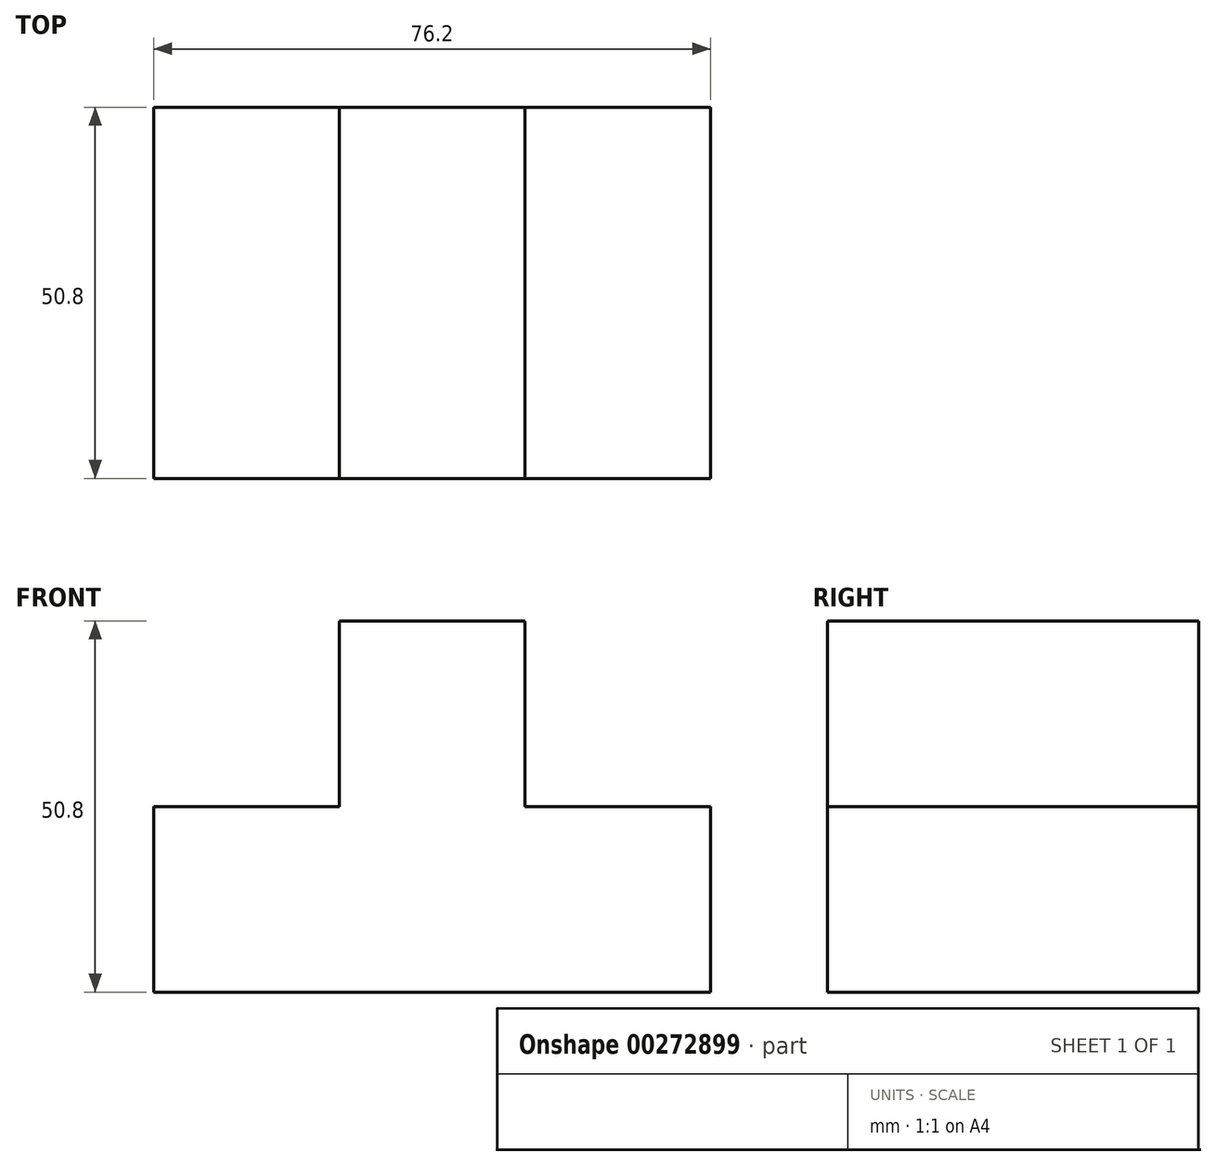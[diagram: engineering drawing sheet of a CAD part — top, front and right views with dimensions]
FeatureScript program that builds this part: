
annotation { "Feature Type Name" : "Feature", "Feature Type Description" : "" }
export const myFeature = defineFeature(function(context is Context, id is Id, definition is map)
    precondition{}
    {
        {
            var Q0;
            Q0=qCreatedBy(makeId("Front.planeOp"),FACE);
            var sketch = newSketch(context, id + "F0", { "sketchPlane" : qUnion([Q0])});
            skLineSegment(sketch, "E0", {"start": v(0, 0) * mm, "end": v(-76.2, 0) * mm});
            skLineSegment(sketch, "E1", {"start": v(-76.2, 25.4) * mm, "end": v(-76.2, 0) * mm});
            skLineSegment(sketch, "E2", {"start": v(-76.2, 25.4) * mm, "end": v(-50.8, 25.4) * mm});
            skLineSegment(sketch, "E3", {"start": v(-50.8, 50.8) * mm, "end": v(-50.8, 25.4) * mm});
            skLineSegment(sketch, "E4", {"start": v(-50.8, 50.8) * mm, "end": v(-25.4, 50.8) * mm});
            skLineSegment(sketch, "E5", {"start": v(-25.4, 25.4) * mm, "end": v(-25.4, 50.8) * mm});
            skLineSegment(sketch, "E6", {"start": v(-25.4, 25.4) * mm, "end": v(0, 25.4) * mm});
            skLineSegment(sketch, "E7", {"start": v(0, 25.4) * mm, "end": v(0, 0) * mm});
            skSolve(sketch);
        }
        {
            var Q0;
            Q0 = qSketchRegion(id + "F0", true);
            extrude(context, id + "F1", {"entities" : qUnion([Q0]), "depth" : 50.8 * mm});
        }
    });
